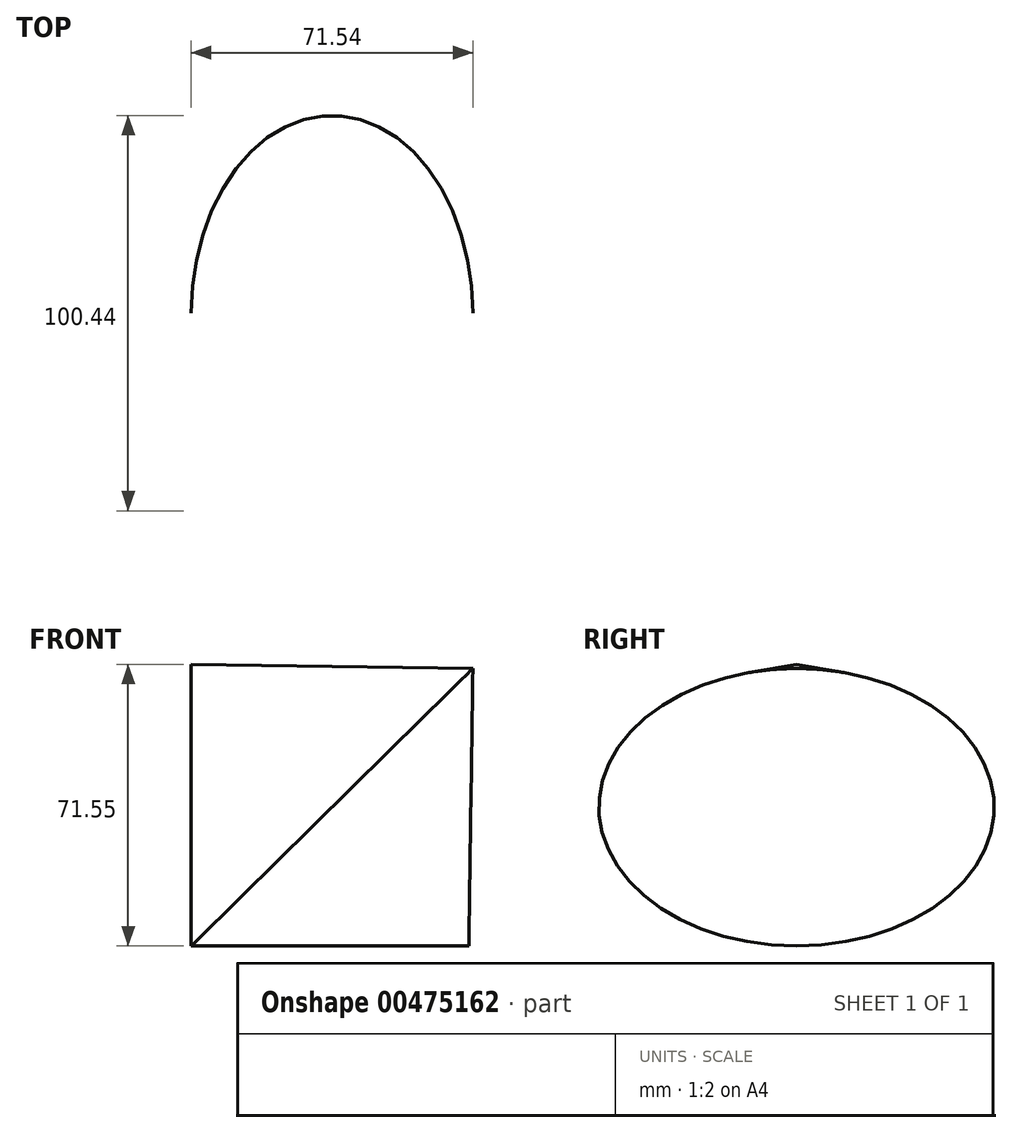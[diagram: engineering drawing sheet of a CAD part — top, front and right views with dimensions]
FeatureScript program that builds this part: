
annotation { "Feature Type Name" : "Feature", "Feature Type Description" : "" }
export const myFeature = defineFeature(function(context is Context, id is Id, definition is map)
    precondition{}
    {
        {
            var Q0;
            Q0=qCreatedBy(makeId("Front.planeOp"),FACE);
            var sketch = newSketch(context, id + "F0", { "sketchPlane" : qUnion([Q0])});
            skLineSegment(sketch, "E0", {"start": v(0, 0) * mm, "end": v(70.5, 0) * mm});
            skLineSegment(sketch, "E1", {"start": v(70.5, 0) * mm, "end": v(0, 71.55) * mm});
            skLineSegment(sketch, "E2", {"start": v(0, 71.55) * mm, "end": v(0, 0) * mm});
            skSolve(sketch);
        }
        {
            var Q0;
            Q0 = qSketchRegion(id + "F0", true);
            var Q1;
            Q1=sQuery(id+"F0.wireOp",EDGE,"E1");
            revolve(context, id + "F1", {"entities" : qUnion([Q0]), "axis" : qUnion([Q1]), "revolveType" : RevolveType.FULL});
        }
    });
